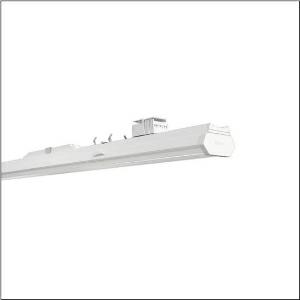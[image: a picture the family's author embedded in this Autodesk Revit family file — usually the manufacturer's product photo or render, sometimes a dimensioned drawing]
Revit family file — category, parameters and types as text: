
# Revit family: licross_11_protected_ho_51td1bmn4fxm
name_source: partatom
category: Lighting Fixtures
units: mm (PartAtom-declared; Revit-internal decimal feet)

## family parameters
Cut with Voids When Loaded = No
Host = Face
Light Source = No
Part Type = Normal
Room Calculation Point = No
Round Connector Dimension = Use Diameter
Shared = No

## types (1)
- --- (1 x LED, 15020 lm, 87.4 W, 4000K)
    Apparent Load = 87 VA
    CIE Flux Codes = 54 82 95 97 100
    Color Rendering = 80
    Color Temperature = 4000K
    Default Elevation = 1800 mm
    Description = Licross 11 Protected HO, luminaire insert, of sheet steel, galvanised, coil coated, white, length: 1.500mm, width: 90mm, height: 101mm, LED rated luminous flux: 15.020lm, light colour: 840, SDCM (Standard Deviation of Colour Matching)MacAdam ≤ 2 SDCM (initial), control gear: ON/OFF Multilumen, with plug, 3-pole, with phase selection, mains connection: 220..240V, AC, 50/60Hz, rated input power: 87W, internal wiring halogen-free, primary optical cover: cover, of PMMA, light emission: direct distribution, primary light characteristic: symmetric, protection rating (complete): IP54, insulation class (complete): insulation class I (protective earthing), certification: CE, ENEC, VDE, UKCA, protection symbol: D if used in an environment with non-conductive dust loads with corresponding accessories, impact resistance: IK06, permissible ambient temperature for indoor applications: -35..+35°C, corresponds to IFS (International Featured Standards) requirements for safety and quality in the food industry, reducing of maximum allowable ambient temperature of 5°C with ceiling mounting, LABS conformity tested according to VDMA 24364:2018-05, The light source and the operating device comply with the requirements of the Ecodesign Regulation (EU) 2019/2020 and are replaceable in accordance with this regulation, packaging unit: 1 piece
    Height = 92 mm
    Lamp = 1 x LED
    Lamp Light Flux = 15020 lm
    Lamp Power = 87.4 W
    Lamp count = 1
    Length = 1500 mm
    Luminous efficacy = 172 lm/W
    Manufacturer = Siteco
    ModVariant = No
    Model = 51TD1BMN4FXM
    Mounting Place = Ceiling
    Mounting Type = Pendant
    Number of Poles = 1
    OnlyDefault = Yes
    Power Factor = 1
    Product Name = Licross 11 Protected HO
    Product group = luminaire insert | ceiling pendant
    ProductGroupID = 901
    Protection Class = Protection class I
    Protection Degree = IP 54
    RLX_Detail_Level = 1
    RLX_Emergency_Light_Flux = 0 lm
    RLX_Emergency_Type = 0
    RLX_Emergency_Type_DB = No
    RlxData = <blob elided: 22229 chars, md5=0e1bde11>
    Socket = socket
    Standby Power = 0 W
    System Light Flux = 15020 lm
    System Power = 87 W
    Type Comments = factory setting: luminous flux: 100 % | (A | C | E) | 203 mA
    Type Image = l_1256145.jpg
    URL = http://relux.com
    VarID = @adj_090539
    Voltage = 0 V
    Weight = 0.00 kg
    Width = 88 mm

## geometry (parser evidence)
native form markers: Blend x4, Sweep x10
no freeform markers — native parametric forms only
